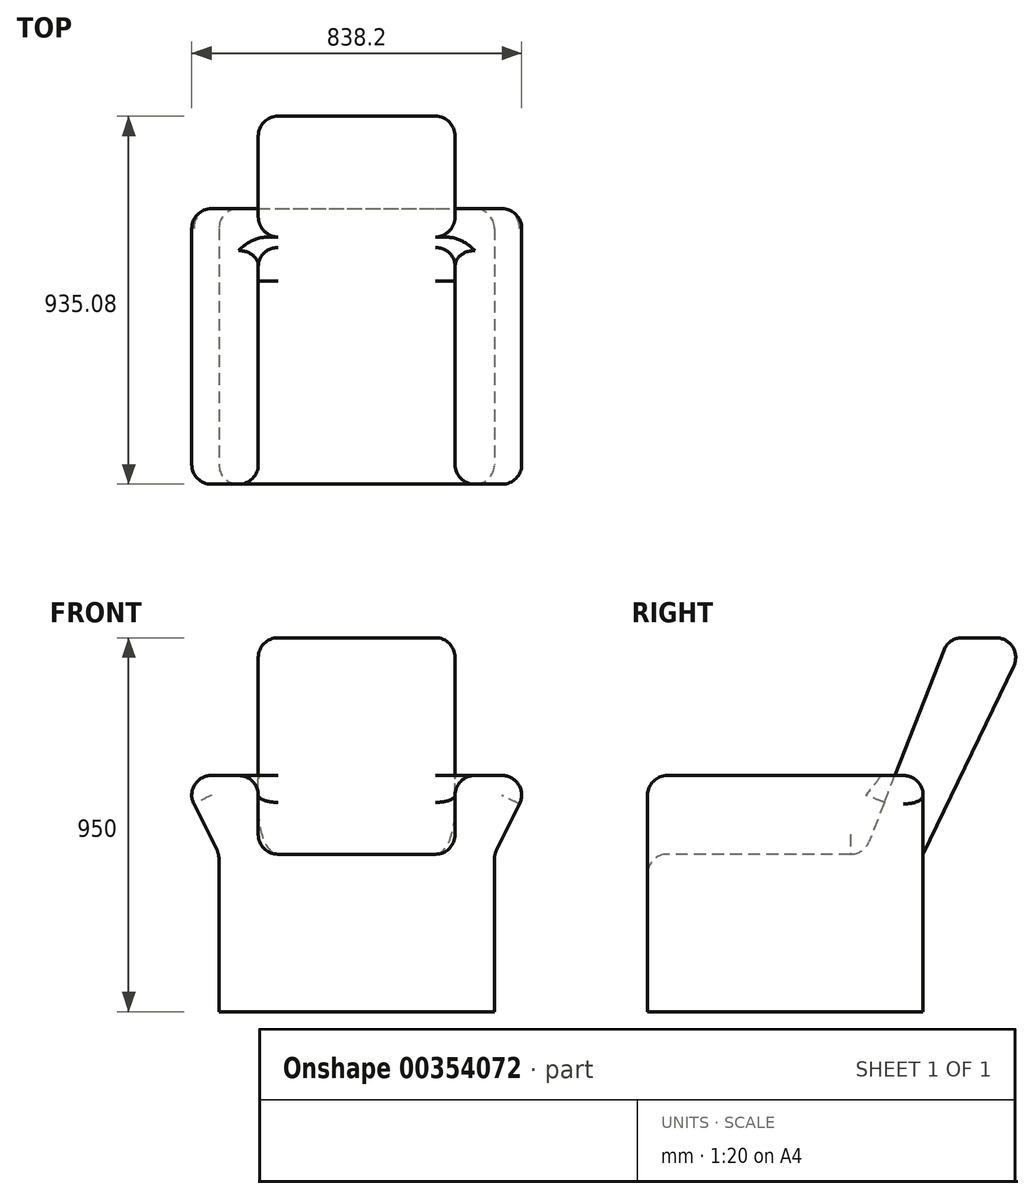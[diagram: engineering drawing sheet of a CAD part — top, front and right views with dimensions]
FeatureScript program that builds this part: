
annotation { "Feature Type Name" : "Feature", "Feature Type Description" : "" }
export const myFeature = defineFeature(function(context is Context, id is Id, definition is map)
    precondition{}
    {
        {
            var Q0;
            Q0=qCreatedBy(makeId("Front.planeOp"),FACE);
            var sketch = newSketch(context, id + "F0", { "sketchPlane" : qUnion([Q0])});
            skLineSegment(sketch, "E0.bottom", {"start": v(-350, 0) * mm, "end": v(350, 0) * mm});
            skLineSegment(sketch, "E0.top", {"start": v(-350, 400) * mm, "end": v(350, 400) * mm});
            skLineSegment(sketch, "E0.left", {"start": v(-350, 0) * mm, "end": v(-350, 400) * mm});
            skLineSegment(sketch, "E0.right", {"start": v(350, 0) * mm, "end": v(350, 400) * mm});
            skLineSegment(sketch, "E1", {"start": v(-250, 400) * mm, "end": v(-250, 600) * mm});
            skLineSegment(sketch, "E2", {"start": v(-250, 600) * mm, "end": v(-450, 600) * mm});
            skLineSegment(sketch, "E3", {"start": v(-450, 600) * mm, "end": v(-350, 400) * mm});
            skLineSegment(sketch, "E4", {"start": v(250, 400) * mm, "end": v(250, 600) * mm});
            skLineSegment(sketch, "E5", {"start": v(250, 600) * mm, "end": v(450, 600) * mm});
            skLineSegment(sketch, "E6", {"start": v(450, 600) * mm, "end": v(350, 400) * mm});
            skSolve(sketch);
        }
        {
            var Q0;
            Q0 = qSketchRegion(id + "F0", true);
            extrude(context, id + "F1", {"entities" : qUnion([Q0]), "oppositeDirection" : true, "depth" : 700 * mm});
        }
        {
            var Q0;
            Q0=qCreatedBy(makeId("Right.planeOp"),FACE);
            var sketch = newSketch(context, id + "F2", { "sketchPlane" : qUnion([Q0])});
            skLineSegment(sketch, "E7", {"start": v(700, 400) * mm, "end": v(964.63, 950) * mm});
            skLineSegment(sketch, "E8", {"start": v(964.63, 950) * mm, "end": v(764.63, 950) * mm});
            skLineSegment(sketch, "E9", {"start": v(764.63, 950) * mm, "end": v(550, 400) * mm});
            skLineSegment(sketch, "E10", {"start": v(550, 400) * mm, "end": v(700, 400) * mm});
            skSolve(sketch);
        }
        {
            var Q0;
            Q0=makeQuery(id+"F2.imprint","IMPRINT",FACE,{"disambiguationData":[TD([[makeQuery(id+"F2.imprint","IMPRINT",EDGE,{"derivedFrom":sQuery(id+"F2.wireOp",EDGE,"E7")}),1.0]])]});
            extrude(context, id + "F3", {"entities" : qUnion([Q0]), "operationType" : NewBodyOperationType.ADD, "endBound" : BoundingType.SYMMETRIC, "oppositeDirection" : true, "depth" : 500 * mm});
        }
        {
            var Q0;
            Q0=makeQuery(id+"F1.opExtrude","SWEPT_EDGE",EDGE,{"disambiguationData":[OSD([sQuery(id+"F0.wireOp",EDGE,"E5"),sQuery(id+"F0.wireOp",EDGE,"E6")])]});
            var Q1;
            Q1=makeQuery(id+"F1.opExtrude","SWEPT_EDGE",EDGE,{"disambiguationData":[OSD([sQuery(id+"F0.wireOp",EDGE,"E2"),sQuery(id+"F0.wireOp",EDGE,"E3")])]});
            var Q2;
            {var subQ0=sQuery(id+"F0.wireOp",EDGE,"E4");var subQ1=sQuery(id+"F0.wireOp",EDGE,"E5");Q2=makeQuery(id+"F3.boolean.opBoolean","SPLIT",EDGE,{"disambiguationData":[topologyDisambiguationEdgeConnected([makeQuery(id+"F1.opExtrude","SWEPT_FACE",FACE,{"disambiguationData":[OSD([subQ0])]})])],"derivedFrom":makeQuery(id+"F1.opExtrude","SWEPT_EDGE",EDGE,{"disambiguationData":[OSD([subQ0,subQ1])]})});}
            var Q3;
            Q3=makeQuery(id+"F3.opExtrude","SWEPT_EDGE",EDGE,{"disambiguationData":[OSD([sQuery(id+"F2.wireOp",EDGE,"E8"),sQuery(id+"F2.wireOp",EDGE,"E9")])]});
            var Q4;
            {var subQ0=sQuery(id+"F0.wireOp",EDGE,"E1");var subQ1=sQuery(id+"F0.wireOp",EDGE,"E2");Q4=makeQuery(id+"F3.boolean.opBoolean","SPLIT",EDGE,{"disambiguationData":[topologyDisambiguationEdgeConnected([makeQuery(id+"F1.opExtrude","SWEPT_FACE",FACE,{"disambiguationData":[OSD([subQ0])]})])],"derivedFrom":makeQuery(id+"F1.opExtrude","SWEPT_EDGE",EDGE,{"disambiguationData":[OSD([subQ0,subQ1])]})});}
            var Q5;
            Q5=makeQuery(id+"F1.opExtrude","CAP_EDGE",EDGE,{"disambiguationData":[OSD([sQuery(id+"F0.wireOp",EDGE,"E5")])],"isStart":false});
            var Q6;
            Q6=makeQuery(id+"F1.opExtrude","CAP_EDGE",EDGE,{"disambiguationData":[OSD([sQuery(id+"F0.wireOp",EDGE,"E2")])],"isStart":false});
            var Q7;
            Q7=makeQuery(id+"F3.opExtrude","SWEPT_EDGE",EDGE,{"disambiguationData":[OSD([sQuery(id+"F2.wireOp",EDGE,"E7"),sQuery(id+"F2.wireOp",EDGE,"E8")])]});
            fillet(context, id + "F4", {"entities" : qUnion([Q0, Q1, Q2, Q3, Q4, Q5, Q6, Q7]), "radius" : 50 * mm, "tangentPropagation" : true, "allowEdgeOverflow" : false});
        }
        {
            var Q0;
            Q0=makeQuery(id+"F1.opExtrude","SWEPT_EDGE",EDGE,{"disambiguationData":[OSD([sQuery(id+"F0.wireOp",EDGE,"E0.top"),sQuery(id+"F0.wireOp",EDGE,"E0.right"),sQuery(id+"F0.wireOp",EDGE,"E6")])]});
            var Q1;
            Q1=makeQuery(id+"F1.opExtrude","SWEPT_EDGE",EDGE,{"disambiguationData":[OSD([sQuery(id+"F0.wireOp",EDGE,"E0.top"),sQuery(id+"F0.wireOp",EDGE,"E0.left"),sQuery(id+"F0.wireOp",EDGE,"E3")])]});
            var Q2;
            Q2=makeQuery(id+"F1.opExtrude","SWEPT_EDGE",EDGE,{"disambiguationData":[OSD([sQuery(id+"F0.wireOp",EDGE,"E0.top"),sQuery(id+"F0.wireOp",EDGE,"E1")])]});
            var Q3;
            Q3=makeQuery(id+"F1.opExtrude","SWEPT_EDGE",EDGE,{"disambiguationData":[OSD([sQuery(id+"F0.wireOp",EDGE,"E0.top"),sQuery(id+"F0.wireOp",EDGE,"E4")])]});
            fillet(context, id + "F5", {"entities" : qUnion([Q0, Q1, Q2, Q3]), "radius" : 50 * mm, "tangentPropagation" : true, "allowEdgeOverflow" : false});
        }
        {
            var Q0;
            Q0=makeQuery(id+"F1.opExtrude","CAP_EDGE",EDGE,{"disambiguationData":[OSD([sQuery(id+"F0.wireOp",EDGE,"E0.right")])],"isStart":true});
            var Q1;
            {var subQ0=sQuery(id+"F0.wireOp",EDGE,"E1");var subQ1=sQuery(id+"F0.wireOp",EDGE,"E2");Q1=makeQuery(id+"F4.opFillet","BLEND_EDGE",EDGE,{"blendedFrom":[makeQuery(id+"F3.boolean.opBoolean","SPLIT",EDGE,{"disambiguationData":[topologyDisambiguationEdgeConnected([makeQuery(id+"F1.opExtrude","SWEPT_FACE",FACE,{"disambiguationData":[OSD([subQ0])]})])],"derivedFrom":makeQuery(id+"F1.opExtrude","SWEPT_EDGE",EDGE,{"disambiguationData":[OSD([subQ0,subQ1])]})}),makeQuery(id+"F3.opExtrude","SWEPT_FACE",FACE,{"disambiguationData":[OSD([sQuery(id+"F2.wireOp",EDGE,"E9")])]})],"blendedInto":[makeQuery(id+"F3.opExtrude","SWEPT_FACE",FACE,{"disambiguationData":[OSD([sQuery(id+"F2.wireOp",EDGE,"E9")])]})]});}
            fillet(context, id + "F6", {"entities" : qUnion([Q0, Q1]), "radius" : 50 * mm, "tangentPropagation" : true, "allowEdgeOverflow" : false});
        }
        {
            var Q0;
            {var subQ0=sQuery(id+"F2.wireOp",EDGE,"E9");Q0=makeQuery(id+"F3.boolean.opBoolean","SPLIT",EDGE,{"disambiguationData":[topologyDisambiguationEdgeConnected([makeQuery(id+"F3.opExtrude","CAP_FACE",FACE,{"disambiguationData":[OSD([sQuery(id+"F2.wireOp",EDGE,"E7"),sQuery(id+"F2.wireOp",EDGE,"E8"),subQ0,sQuery(id+"F2.wireOp",EDGE,"E10")])],"isStart":true})])],"derivedFrom":makeQuery(id+"F3.opExtrude","CAP_EDGE",EDGE,{"disambiguationData":[OSD([subQ0])],"isStart":true})});}
            var Q1;
            {var subQ0=sQuery(id+"F2.wireOp",EDGE,"E9");Q1=makeQuery(id+"F3.boolean.opBoolean","SPLIT",EDGE,{"disambiguationData":[topologyDisambiguationEdgeConnected([makeQuery(id+"F3.opExtrude","CAP_FACE",FACE,{"disambiguationData":[OSD([sQuery(id+"F2.wireOp",EDGE,"E7"),sQuery(id+"F2.wireOp",EDGE,"E8"),subQ0,sQuery(id+"F2.wireOp",EDGE,"E10")])],"isStart":false})])],"derivedFrom":makeQuery(id+"F3.opExtrude","CAP_EDGE",EDGE,{"disambiguationData":[OSD([subQ0])],"isStart":false})});}
            fillet(context, id + "F7", {"entities" : qUnion([Q0, Q1]), "radius" : 50 * mm, "tangentPropagation" : true, "allowEdgeOverflow" : false});
        }
        {
            var Q0;
            Q0=makeQuery(id+"F1.opExtrude","CAP_EDGE",EDGE,{"disambiguationData":[OSD([sQuery(id+"F0.wireOp",EDGE,"E0.right")])],"isStart":false});
            var Q1;
            Q1=makeQuery(id+"F1.opExtrude","CAP_EDGE",EDGE,{"disambiguationData":[OSD([sQuery(id+"F0.wireOp",EDGE,"E0.left")])],"isStart":false});
            fillet(context, id + "F8", {"entities" : qUnion([Q0, Q1]), "radius" : 50 * mm, "tangentPropagation" : true, "allowEdgeOverflow" : false});
        }
    });
